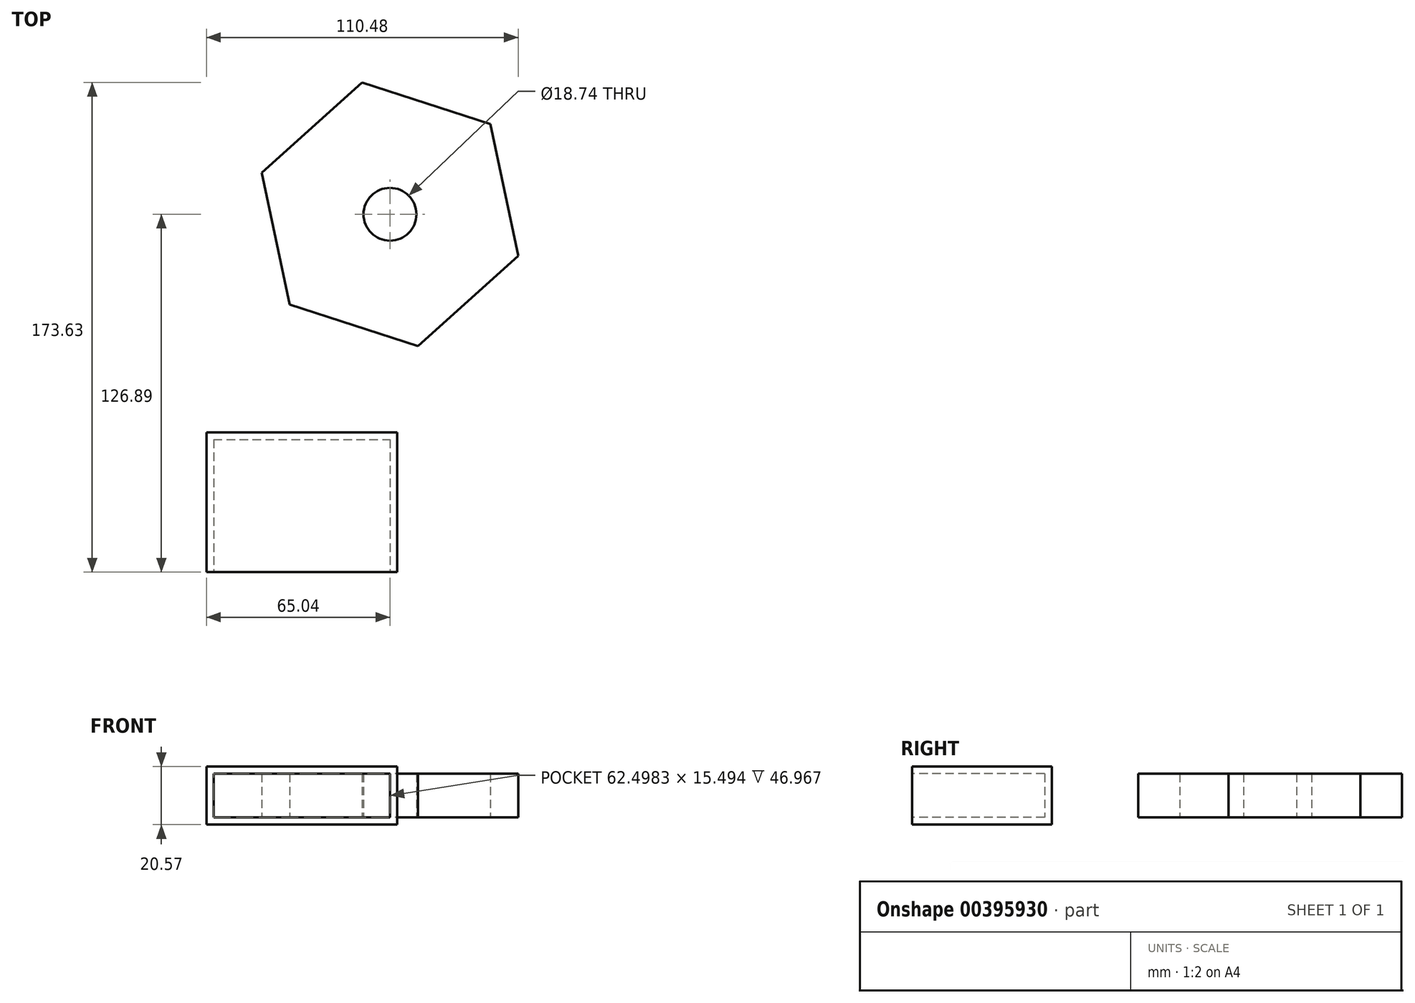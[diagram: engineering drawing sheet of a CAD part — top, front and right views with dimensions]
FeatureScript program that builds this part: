
annotation { "Feature Type Name" : "Feature", "Feature Type Description" : "" }
export const myFeature = defineFeature(function(context is Context, id is Id, definition is map)
    precondition{}
    {
        {
            var Q0;
            Q0=qCreatedBy(makeId("Top.planeOp"),FACE);
            var sketch = newSketch(context, id + "F0", { "sketchPlane" : qUnion([Q0])});
            skCircle(sketch, "E0.cCircle", {"center": v(0, 0) * mm, "radius": 41.38 * mm, "construction": true});
            skLineSegment(sketch, "E0.0", {"start": v(-35.52, -31.96) * mm, "end": v(9.92, -46.74) * mm});
            skLineSegment(sketch, "E0.1", {"start": v(-45.44, 14.78) * mm, "end": v(-35.52, -31.96) * mm});
            skLineSegment(sketch, "E0.2", {"start": v(-9.92, 46.74) * mm, "end": v(-45.44, 14.78) * mm});
            skLineSegment(sketch, "E0.3", {"start": v(35.52, 31.96) * mm, "end": v(-9.92, 46.74) * mm});
            skLineSegment(sketch, "E0.4", {"start": v(45.44, -14.78) * mm, "end": v(35.52, 31.96) * mm});
            skLineSegment(sketch, "E0.5", {"start": v(9.92, -46.74) * mm, "end": v(45.44, -14.78) * mm});
            skPoint(sketch, "E0.0.midPoint", {"position": v(-12.8, -39.35) * mm});
            skCircle(sketch, "E1", {"center": v(0, 0) * mm, "radius": 9.37 * mm});
            skLineSegment(sketch, "E2.bottom", {"start": v(-62.5, -79.92) * mm, "end": v(0, -79.92) * mm});
            skLineSegment(sketch, "E2.top", {"start": v(-62.5, -126.89) * mm, "end": v(0, -126.89) * mm});
            skLineSegment(sketch, "E2.left", {"start": v(-62.5, -79.92) * mm, "end": v(-62.5, -126.89) * mm});
            skLineSegment(sketch, "E2.right", {"start": v(0, -79.92) * mm, "end": v(0, -126.89) * mm});
            skSolve(sketch);
        }
        {
            var Q0;
            Q0 = qSketchRegion(id + "F0", true);
            extrude(context, id + "F1", {"entities" : qUnion([Q0]), "depth" : 15.5 * mm});
        }
        {
            var Q0;
            Q0=makeQuery(id+"F1.opExtrude","SWEPT_FACE",FACE,{"disambiguationData":[OSD([sQuery(id+"F0.wireOp",EDGE,"E2.top")])]});
            shell(context, id + "F2", {"entities" : qUnion([Q0]), "thickness" : 2.54 * mm, "oppositeDirection" : true});
        }
    });
